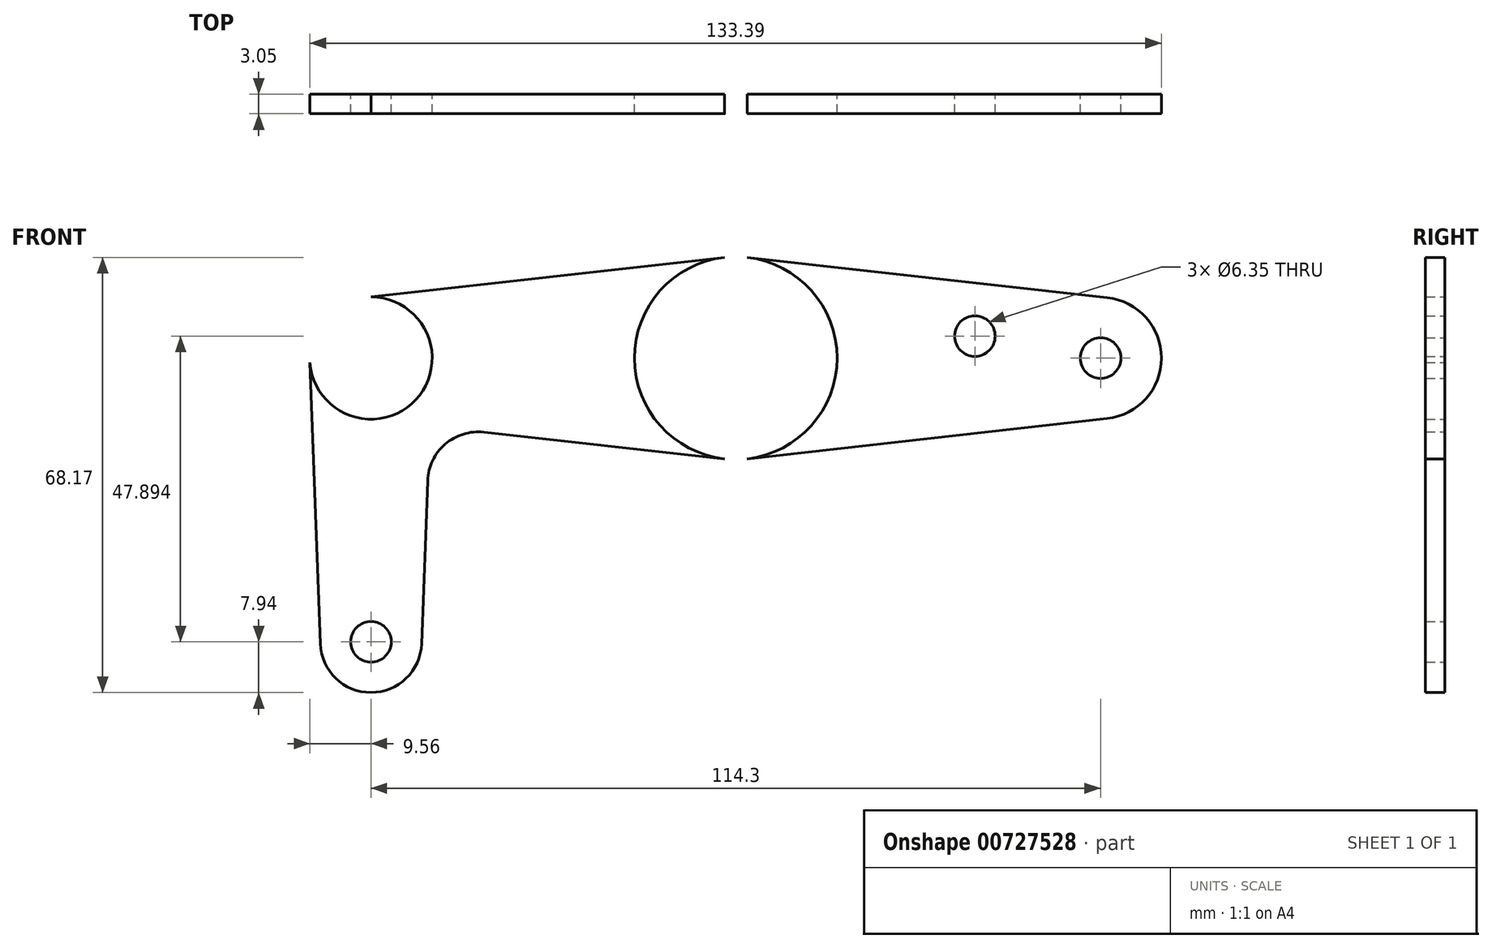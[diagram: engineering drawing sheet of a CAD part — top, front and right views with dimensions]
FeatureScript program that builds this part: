
annotation { "Feature Type Name" : "Feature", "Feature Type Description" : "" }
export const myFeature = defineFeature(function(context is Context, id is Id, definition is map)
    precondition{}
    {
        {
            var Q0;
            Q0=qCreatedBy(makeId("Front.planeOp"),FACE);
            var sketch = newSketch(context, id + "F0", { "sketchPlane" : qUnion([Q0])});
            skLineSegment(sketch, "E0", {"start": v(0, 0) * mm, "end": v(114.3, 0) * mm});
            skLineSegment(sketch, "E1", {"start": v(114.3, 0) * mm, "end": v(0, 0) * mm});
            skLineSegment(sketch, "E2", {"start": v(0, 0) * mm, "end": v(0, -44.45) * mm});
            skCircle(sketch, "E3", {"center": v(57.15, 0) * mm, "radius": 15.88 * mm});
            skCircle(sketch, "E4", {"center": v(114.3, 0) * mm, "radius": 9.53 * mm});
            skCircle(sketch, "E5", {"center": v(0, -44.45) * mm, "radius": 7.94 * mm});
            skLineSegment(sketch, "E6", {"start": v(115.36, 9.47) * mm, "end": v(58.91, 15.78) * mm});
            skLineSegment(sketch, "E7", {"start": v(115.36, -9.47) * mm, "end": v(58.91, -15.78) * mm});
            skLineSegment(sketch, "E8", {"start": v(8.88, -19.21) * mm, "end": v(7.93, -44.74) * mm});
            skLineSegment(sketch, "E9", {"start": v(-9.58, 0) * mm, "end": v(-7.93, -44.74) * mm});
            skCircle(sketch, "E10", {"center": v(0, 0) * mm, "radius": 9.58 * mm});
            skLineSegment(sketch, "E11", {"start": v(55.4, -15.78) * mm, "end": v(17.7, -11.6) * mm});
            skLineSegment(sketch, "E12", {"start": v(55.39, 15.78) * mm, "end": v(0, 9.58) * mm});
            skCircle(sketch, "E13", {"center": v(114.3, 0) * mm, "radius": 3.18 * mm});
            skCircle(sketch, "E14", {"center": v(57.15, 0) * mm, "radius": 3.18 * mm});
            skCircle(sketch, "E15", {"center": v(0, 0) * mm, "radius": 3.18 * mm});
            skCircle(sketch, "E16", {"center": v(0, -44.45) * mm, "radius": 3.18 * mm});
            skArc(sketch, "E17.filletArc", {"start": v(17.7, -11.6) * mm, "mid": v(11.63, -13.48) * mm, "end": v(8.88, -19.21) * mm});
            skCircle(sketch, "E18", {"center": v(94.6, 3.44) * mm, "radius": 3.18 * mm});
            skSolve(sketch);
        }
        {
            var Q0;
            {var subQ0=sQuery(id+"F0.wireOp",EDGE,"E10");var subQ2=sQuery(id+"F0.wireOp",EDGE,"E1");var subQ3=makeQuery(id+"F0.imprint","INTERSECT",VERTEX,{"derivedFrom":[subQ2,subQ0]});Q0=makeQuery(id+"F0.imprint","IMPRINT",FACE,{"disambiguationData":[TD([[makeQuery(id+"F0.imprint","IMPRINT",EDGE,{"disambiguationData":[TD([[subQ3,-1.0]])],"derivedFrom":subQ2}),-1.0]])]});}
            var Q1;
            {var subQ0=sQuery(id+"F0.wireOp",EDGE,"E8");Q1=makeQuery(id+"F0.imprint","IMPRINT",FACE,{"disambiguationData":[TD([[makeQuery(id+"F0.imprint","IMPRINT",EDGE,{"derivedFrom":subQ0}),-1.0]])]});}
            var Q2;
            {var subQ5=sQuery(id+"F0.wireOp",EDGE,"E12");Q2=makeQuery(id+"F0.imprint","IMPRINT",FACE,{"disambiguationData":[TD([[makeQuery(id+"F0.imprint","IMPRINT",EDGE,{"derivedFrom":subQ5}),1.0]])]});}
            var Q3;
            {var subQ0=sQuery(id+"F0.wireOp",EDGE,"E10");var subQ1=sQuery(id+"F0.wireOp",EDGE,"E1");var subQ2=makeQuery(id+"F0.imprint","INTERSECT",VERTEX,{"derivedFrom":[subQ1,subQ0]});Q3=makeQuery(id+"F0.imprint","IMPRINT",FACE,{"disambiguationData":[TD([[makeQuery(id+"F0.imprint","IMPRINT",EDGE,{"disambiguationData":[TD([[subQ2,-1.0]])],"derivedFrom":subQ1}),1.0]])]});}
            var Q4;
            {var subQ0=sQuery(id+"F0.wireOp",EDGE,"E3");var subQ2=sQuery(id+"F0.wireOp",EDGE,"E1");var subQ3=makeQuery(id+"F0.imprint","INTERSECT",VERTEX,{"disambiguationData":[OD(0.0)],"derivedFrom":[subQ2,subQ0]});Q4=makeQuery(id+"F0.imprint","IMPRINT",FACE,{"disambiguationData":[TD([[makeQuery(id+"F0.imprint","IMPRINT",EDGE,{"disambiguationData":[TD([[subQ3,-1.0]])],"derivedFrom":subQ2}),-1.0]])]});}
            var Q5;
            {var subQ0=sQuery(id+"F0.wireOp",EDGE,"E3");var subQ4=sQuery(id+"F0.wireOp",EDGE,"E1");var subQ8=makeQuery(id+"F0.imprint","INTERSECT",VERTEX,{"disambiguationData":[OD(0.0)],"derivedFrom":[subQ4,subQ0]});Q5=makeQuery(id+"F0.imprint","IMPRINT",FACE,{"disambiguationData":[TD([[makeQuery(id+"F0.imprint","IMPRINT",EDGE,{"disambiguationData":[TD([[subQ8,-1.0]])],"derivedFrom":subQ4}),1.0]])]});}
            var Q6;
            {var subQ5=sQuery(id+"F0.wireOp",EDGE,"E7");Q6=makeQuery(id+"F0.imprint","IMPRINT",FACE,{"disambiguationData":[TD([[makeQuery(id+"F0.imprint","IMPRINT",EDGE,{"derivedFrom":subQ5}),-1.0]])]});}
            var Q7;
            {var subQ0=sQuery(id+"F0.wireOp",EDGE,"E6");Q7=makeQuery(id+"F0.imprint","IMPRINT",FACE,{"disambiguationData":[TD([[makeQuery(id+"F0.imprint","IMPRINT",EDGE,{"derivedFrom":subQ0}),1.0]])]});}
            var Q8;
            Q8=makeQuery(id+"F0.imprint","IMPRINT",FACE,{"disambiguationData":[TD([[makeQuery(id+"F0.imprint","IMPRINT",EDGE,{"derivedFrom":sQuery(id+"F0.wireOp",EDGE,"E13")}),-1.0]])]});
            var Q9;
            {var subQ0=sQuery(id+"F0.wireOp",EDGE,"E5");var subQ1=sQuery(id+"F0.wireOp",EDGE,"E2");var subQ2=makeQuery(id+"F0.imprint","INTERSECT",VERTEX,{"derivedFrom":[subQ1,subQ0]});Q9=makeQuery(id+"F0.imprint","IMPRINT",FACE,{"disambiguationData":[TD([[makeQuery(id+"F0.imprint","IMPRINT",EDGE,{"disambiguationData":[TD([[subQ2,1.0]])],"derivedFrom":subQ1}),-1.0]])]});}
            var Q10;
            Q10=makeQuery(id+"F0.imprint","IMPRINT",FACE,{"disambiguationData":[TD([[makeQuery(id+"F0.imprint","IMPRINT",EDGE,{"derivedFrom":sQuery(id+"F0.wireOp",EDGE,"E16")}),-1.0]])]});
            extrude(context, id + "F1", {"entities" : qUnion([Q0, Q1, Q2, Q3, Q4, Q5, Q6, Q7, Q8, Q9, Q10]), "depth" : 3.05 * mm, "offsetDistance" : 25.4 * mm});
        }
    });
